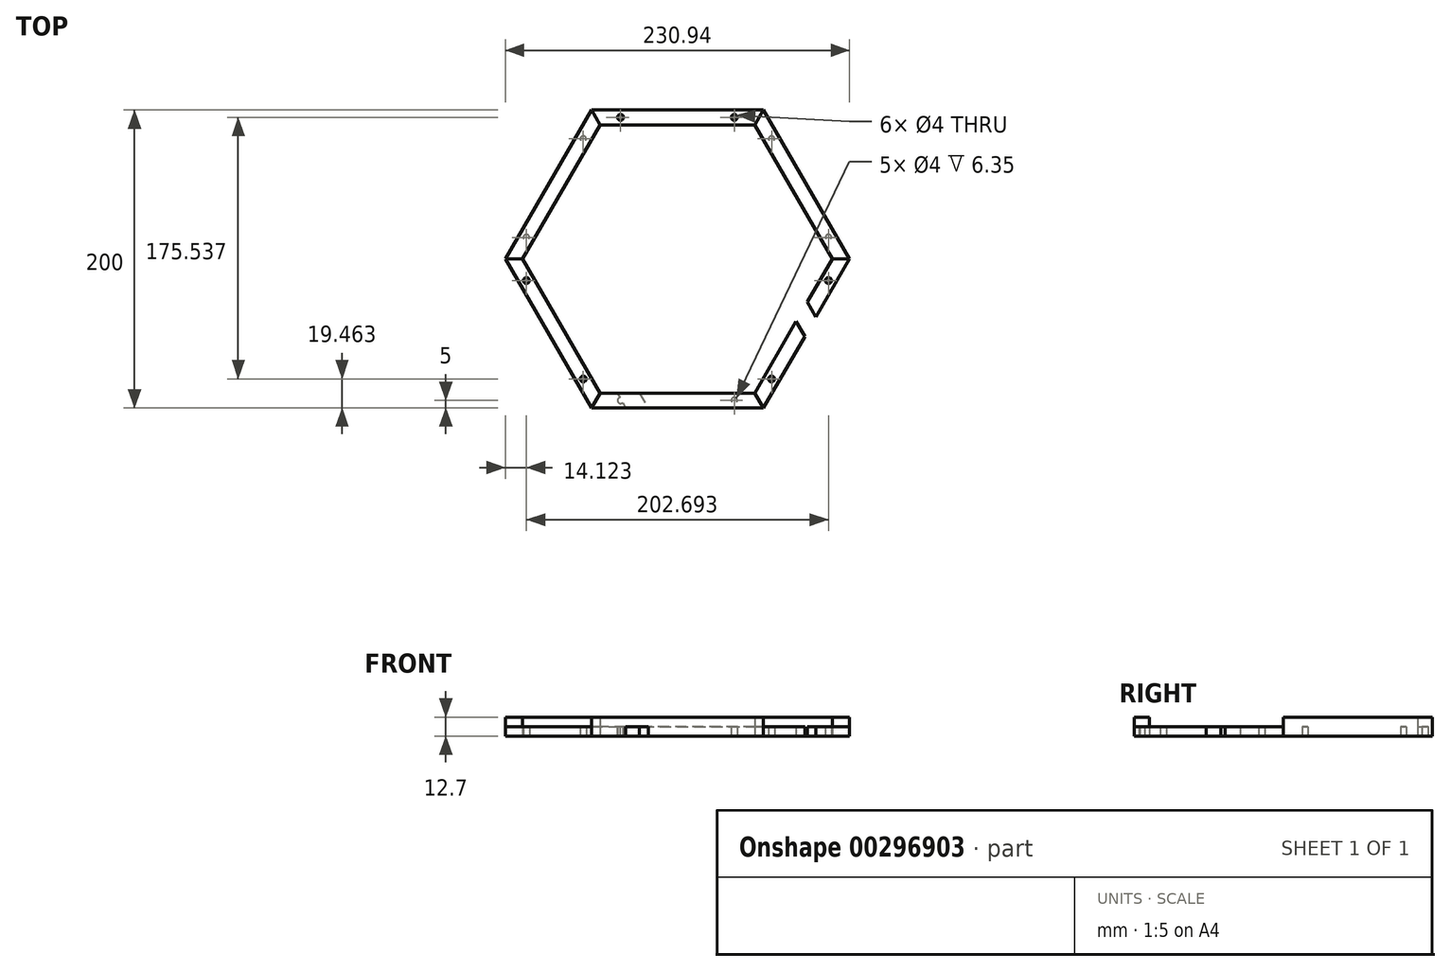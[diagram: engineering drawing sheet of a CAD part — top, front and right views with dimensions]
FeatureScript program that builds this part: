
annotation { "Feature Type Name" : "Feature", "Feature Type Description" : "" }
export const myFeature = defineFeature(function(context is Context, id is Id, definition is map)
    precondition{}
    {
        {
            var Q0;
            Q0=qCreatedBy(makeId("Top.planeOp"),FACE);
            var sketch = newSketch(context, id + "F0", { "sketchPlane" : qUnion([Q0])});
            skCircle(sketch, "E0", {"center": v(0, 0) * mm, "radius": 100 * mm});
            skCircle(sketch, "E1.cCircle", {"center": v(0, 0) * mm, "radius": 100 * mm, "construction": true});
            skLineSegment(sketch, "E1.0", {"start": v(-57.74, 100) * mm, "end": v(57.74, 100) * mm});
            skLineSegment(sketch, "E1.1", {"start": v(57.74, 100) * mm, "end": v(115.47, 0) * mm});
            skLineSegment(sketch, "E1.2", {"start": v(115.47, 0) * mm, "end": v(57.74, -100) * mm});
            skLineSegment(sketch, "E1.3", {"start": v(57.74, -100) * mm, "end": v(-57.74, -100) * mm});
            skLineSegment(sketch, "E1.4", {"start": v(-57.74, -100) * mm, "end": v(-115.47, 0) * mm});
            skLineSegment(sketch, "E1.5", {"start": v(-115.47, 0) * mm, "end": v(-57.74, 100) * mm});
            skPoint(sketch, "E1.0.midPoint", {"position": v(0, 100) * mm});
            skSolve(sketch);
        }
        {
            var Q0;
            Q0=qSketchRegion(id+"F0",true);
            extrude(context, id + "F1", {"entities" : qUnion([Q0]), "depth" : 6.35 * mm});
        }
        {
            var Q0;
            Q0=qCreatedBy(makeId("Top.planeOp"),FACE);
            var sketch = newSketch(context, id + "F2", { "sketchPlane" : qUnion([Q0])});
            skCircle(sketch, "E2.cCircle", {"center": v(0, 0) * mm, "radius": 95 * mm, "construction": true});
            skLineSegment(sketch, "E2.0", {"start": v(-54.85, 95) * mm, "end": v(54.85, 95) * mm, "construction": true});
            skLineSegment(sketch, "E2.1", {"start": v(54.85, 95) * mm, "end": v(109.7, 0) * mm, "construction": true});
            skLineSegment(sketch, "E2.2", {"start": v(109.7, 0) * mm, "end": v(54.85, -95) * mm, "construction": true});
            skLineSegment(sketch, "E2.3", {"start": v(54.85, -95) * mm, "end": v(-54.85, -95) * mm, "construction": true});
            skLineSegment(sketch, "E2.4", {"start": v(-54.85, -95) * mm, "end": v(-109.7, 0) * mm, "construction": true});
            skLineSegment(sketch, "E2.5", {"start": v(-109.7, 0) * mm, "end": v(-54.85, 95) * mm, "construction": true});
            skPoint(sketch, "E2.0.midPoint", {"position": v(0, 95) * mm});
            skPoint(sketch, "E3", {"position": v(38.15, 95) * mm});
            skPoint(sketch, "E4", {"position": v(-38.15, 95) * mm});
            skPoint(sketch, "E5", {"position": v(38.15, -95) * mm});
            skPoint(sketch, "E6", {"position": v(-38.15, -95) * mm});
            skPoint(sketch, "E7", {"position": v(-63.2, -80.54) * mm});
            skPoint(sketch, "E8", {"position": v(-101.35, -14.46) * mm});
            skPoint(sketch, "E9", {"position": v(-101.35, 14.46) * mm});
            skPoint(sketch, "E10", {"position": v(-63.2, 80.54) * mm});
            skPoint(sketch, "E11", {"position": v(63.2, 80.54) * mm});
            skPoint(sketch, "E12", {"position": v(101.35, 14.46) * mm});
            skPoint(sketch, "E13", {"position": v(101.35, -14.46) * mm});
            skPoint(sketch, "E14", {"position": v(63.2, -80.54) * mm});
            skCircle(sketch, "E15", {"center": v(38.15, 95) * mm, "radius": 2 * mm});
            skCircle(sketch, "E16", {"center": v(-38.15, 95) * mm, "radius": 2 * mm});
            skCircle(sketch, "E17", {"center": v(-63.2, 80.54) * mm, "radius": 2 * mm});
            skCircle(sketch, "E18", {"center": v(-101.35, 14.46) * mm, "radius": 2 * mm});
            skCircle(sketch, "E19", {"center": v(-101.35, -14.46) * mm, "radius": 2 * mm});
            skCircle(sketch, "E20", {"center": v(-63.2, -80.54) * mm, "radius": 2 * mm});
            skCircle(sketch, "E21", {"center": v(-38.15, -95) * mm, "radius": 2 * mm});
            skCircle(sketch, "E22", {"center": v(38.15, -95) * mm, "radius": 2 * mm});
            skCircle(sketch, "E23", {"center": v(63.2, -80.54) * mm, "radius": 2 * mm});
            skCircle(sketch, "E24", {"center": v(101.35, -14.46) * mm, "radius": 2 * mm});
            skCircle(sketch, "E25", {"center": v(101.35, 14.46) * mm, "radius": 2 * mm});
            skCircle(sketch, "E26", {"center": v(63.2, 80.54) * mm, "radius": 2 * mm});
            skCircle(sketch, "E27.cCircle", {"center": v(0, 0) * mm, "radius": 90 * mm, "construction": true});
            skLineSegment(sketch, "E27.0", {"start": v(-51.96, 90) * mm, "end": v(51.96, 90) * mm});
            skLineSegment(sketch, "E27.1", {"start": v(51.96, 90) * mm, "end": v(103.92, 0) * mm});
            skLineSegment(sketch, "E27.2", {"start": v(103.92, 0) * mm, "end": v(51.96, -90) * mm});
            skLineSegment(sketch, "E27.3", {"start": v(51.96, -90) * mm, "end": v(-51.96, -90) * mm});
            skLineSegment(sketch, "E27.4", {"start": v(-51.96, -90) * mm, "end": v(-103.92, 0) * mm});
            skLineSegment(sketch, "E27.5", {"start": v(-103.92, 0) * mm, "end": v(-51.96, 90) * mm});
            skPoint(sketch, "E27.0.midPoint", {"position": v(0, 90) * mm});
            skSolve(sketch);
        }
        {
            var Q0;
            Q0=qSketchRegion(id+"F2",true);
            extrude(context, id + "F3", {"entities" : qUnion([Q0]), "operationType" : NewBodyOperationType.REMOVE, "depth" : 20000 * mm});
        }
        {
            var Q0;
            Q0=makeQuery(id+"F1.opExtrude","CAP_FACE",FACE,{"disambiguationData":[OSD([sQuery(id+"F0.wireOp",EDGE,"E1.0"),sQuery(id+"F0.wireOp",EDGE,"E1.1"),sQuery(id+"F0.wireOp",EDGE,"E1.2"),sQuery(id+"F0.wireOp",EDGE,"E1.3"),sQuery(id+"F0.wireOp",EDGE,"E1.4"),sQuery(id+"F0.wireOp",EDGE,"E1.5")])],"isStart":false});
            var sketch = newSketch(context, id + "F4", { "sketchPlane" : qUnion([Q0])});
            skLineSegment(sketch, "E28", {"start": v(-51.96, -90) * mm, "end": v(-43.3, -85) * mm, "construction": true});
            skLineSegment(sketch, "E29", {"start": v(-43.3, -85) * mm, "end": v(-32.04, -78.5) * mm});
            skLineSegment(sketch, "E30", {"start": v(-32.04, -78.5) * mm, "end": v(-18.92, -101.22) * mm});
            skLineSegment(sketch, "E31", {"start": v(-43.3, -85) * mm, "end": v(-31.1, -106.13) * mm});
            skLineSegment(sketch, "E32", {"start": v(-31.1, -106.13) * mm, "end": v(-18.92, -101.22) * mm});
            skLineSegment(sketch, "E33", {"start": v(103.92, 0) * mm, "end": v(78.8, -14.5) * mm, "construction": true});
            skLineSegment(sketch, "E34", {"start": v(78.8, -14.5) * mm, "end": v(67.55, -21) * mm});
            skLineSegment(sketch, "E35", {"start": v(78.8, -14.5) * mm, "end": v(110.67, -69.68) * mm});
            skLineSegment(sketch, "E36", {"start": v(67.55, -21) * mm, "end": v(99.62, -76.55) * mm});
            skLineSegment(sketch, "E37", {"start": v(99.62, -76.55) * mm, "end": v(110.67, -69.68) * mm});
            skSolve(sketch);
        }
        {
            var Q0;
            Q0 = qSketchRegion(id + "F4", true);
            extrude(context, id + "F5", {"entities" : qUnion([Q0]), "operationType" : NewBodyOperationType.REMOVE, "oppositeDirection" : true, "depth" : 25 * mm});
        }
        {
            var Q0;
            {var subQ0=sQuery(id+"F0.wireOp",EDGE,"E1.3");var subQ1=sQuery(id+"F0.wireOp",EDGE,"E1.2");var subQ3=makeQuery(id+"F1.opExtrude","CAP_EDGE",EDGE,{"disambiguationData":[OSD([subQ0])],"isStart":false});var subQ4=makeQuery(id+"F1.opExtrude","CAP_EDGE",EDGE,{"disambiguationData":[OSD([subQ1])],"isStart":false});var subQ5=makeQuery(id+"F4.imprint","INTERSECT",VERTEX,{"derivedFrom":[subQ4,subQ3]});Q0=makeQuery(id+"F4.imprint","IMPRINT",FACE,{"disambiguationData":[TD([[makeQuery(id+"F4.imprint","IMPRINT",EDGE,{"disambiguationData":[TD([[subQ5,1.0]])],"derivedFrom":subQ4}),-1.0]])]});}
            var sketch = newSketch(context, id + "F6", { "sketchPlane" : qUnion([Q0])});
            skLineSegment(sketch, "E38", {"start": v(-57.74, -100) * mm, "end": v(-51.96, -90) * mm});
            skLineSegment(sketch, "E39", {"start": v(115.47, 0) * mm, "end": v(103.92, 0) * mm});
            skLineSegment(sketch, "E40", {"start": v(103.92, 0) * mm, "end": v(51.96, 90) * mm});
            skLineSegment(sketch, "E41", {"start": v(51.96, 90) * mm, "end": v(57.74, 100) * mm});
            skLineSegment(sketch, "E42", {"start": v(57.74, 100) * mm, "end": v(115.47, 0) * mm});
            skLineSegment(sketch, "E43", {"start": v(-115.47, 0) * mm, "end": v(-103.92, 0) * mm});
            skLineSegment(sketch, "E44", {"start": v(-103.92, 0) * mm, "end": v(-51.96, 90) * mm});
            skLineSegment(sketch, "E45", {"start": v(-51.96, 90) * mm, "end": v(-57.74, 100) * mm});
            skLineSegment(sketch, "E46", {"start": v(-57.74, 100) * mm, "end": v(-115.47, 0) * mm});
            skLineSegment(sketch, "E47", {"start": v(-51.96, -90) * mm, "end": v(51.96, -90) * mm});
            skLineSegment(sketch, "E48", {"start": v(-57.74, -100) * mm, "end": v(57.74, -100) * mm});
            skLineSegment(sketch, "E49", {"start": v(57.74, -100) * mm, "end": v(51.96, -90) * mm});
            skSolve(sketch);
        }
        {
            var Q0;
            Q0 = qSketchRegion(id + "F6", true);
            extrude(context, id + "F7", {"entities" : qUnion([Q0]), "operationType" : NewBodyOperationType.ADD, "depth" : 6.35 * mm});
        }
    });
